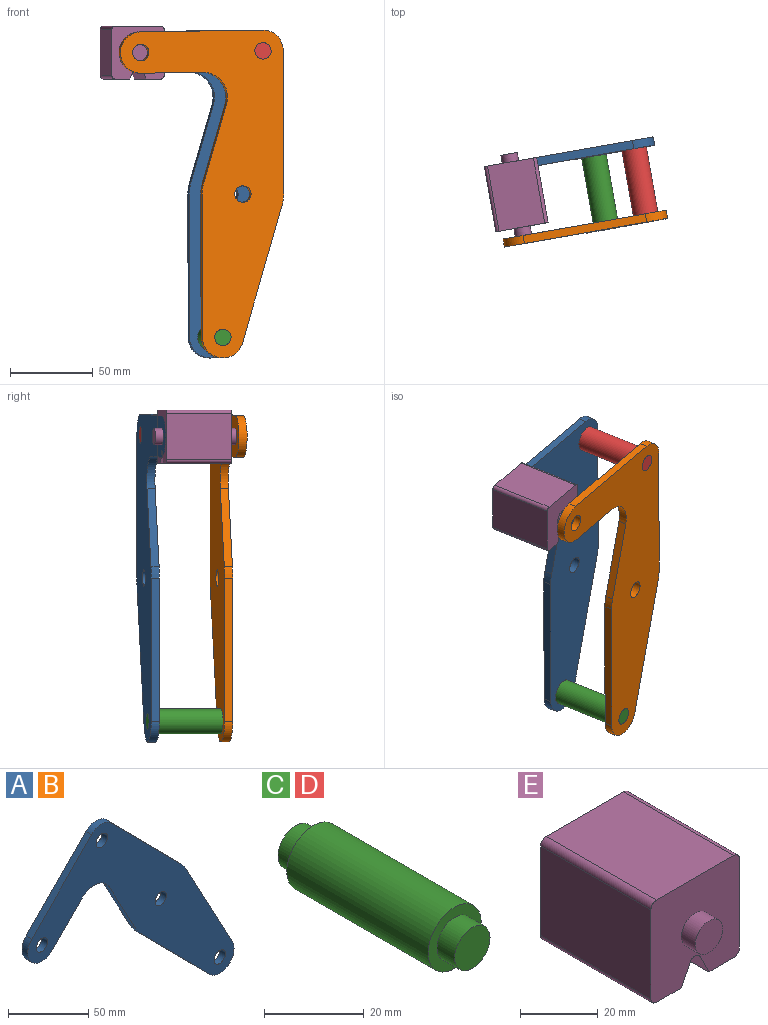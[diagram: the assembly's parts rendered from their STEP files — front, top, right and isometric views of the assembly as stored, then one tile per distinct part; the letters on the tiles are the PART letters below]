
ASSEMBLY  parts=5 mates=3
PART A: 18 faces, bbox 181.7x5x165.8 mm
  f0: plane 43.49x23.35mm, normal (-0.88,0,-0.47), area 246.8mm2, adj f1,f14,f16,f17
  f1: cylinder r=25mm len=5.75mm, axis (0,1,0), area 35.8mm2, adj f0,f2,f16,f17
  f2: plane 61.6x60.87mm, normal (-0.71,0,-0.7), area 433mm2, adj f1,f3,f16,f17
  f3: cylinder r=12.5mm len=21.39mm, axis (0,1,0), area 178.4mm2, adj f2,f4,f16,f17
  f4: plane 76.3x40.96mm, normal (0.88,0,0.47), area 433mm2, adj f3,f5,f16,f17
  f5: cylinder r=25mm len=5.75mm, axis (0,1,0), area 35.8mm2, adj f4,f6,f16,f17
  f6: plane 61.6x60.87mm, normal (0.71,0,0.7), area 433mm2, adj f5,f7,f16,f17
  f7: cylinder r=12.5mm len=17.78mm, axis (0,1,0), area 98.9mm2, adj f6,f8,f16,f17
  f8: plane 53.35x52.71mm, normal (-0.71,0,0.7), area 375mm2, adj f7,f9,f16,f17
  f9: cylinder r=12.5mm len=21.39mm, axis (0,1,0), area 196.3mm2, adj f8,f10,f16,f17
  f10: plane 26.86x26.54mm, normal (0.71,0,-0.7), area 188.8mm2, adj f9,f14,f16,f17
  f11: cylinder r=5mm len=10mm, axis (0,1,0), area 157.1mm2, adj f16,f17
  f12: cylinder r=5mm len=10mm, axis (0,1,0), area 157.1mm2, adj f16,f17
  f13: cylinder r=5mm len=10mm, axis (0,1,0), area 157.1mm2, adj f16,f17
  f14: cylinder r=15mm len=23.89mm, axis (0,1,0), area 140.2mm2, adj f0,f10,f16,f17
  f15: cylinder r=5mm len=10mm, axis (0,1,0), area 157.1mm2, adj f16,f17
  f16: plane 181.66x165.78mm, normal (0,-1,0), area 8710.1mm2, adj f0,f1,f2,f3,f4,f5,f6,f7
  f17: plane 181.66x165.78mm, normal (0,1,0), area 8710.1mm2, adj f0,f1,f2,f3,f4,f5,f6,f7
PART B: same geometry as A
PART C: 7 faces, bbox 15x50x15 mm
  f0: cylinder r=7.5mm len=40mm, axis (0,-1,0), area 1885mm2, adj f2,f5
  f1: cylinder r=5mm len=10mm, axis (0,1,0), area 157.1mm2, adj f2,f3
  f2: plane 15x15mm, normal (0,-1,0), area 98.2mm2, adj f0,f1
  f3: plane 10x10mm, normal (0,-1,0), area 78.5mm2, adj f1
  f4: cylinder r=5mm len=10mm, axis (0,-1,0), area 157.1mm2, adj f5,f6
  f5: plane 15x15mm, normal (0,1,0), area 98.2mm2, adj f0,f4
  f6: plane 10x10mm, normal (0,1,0), area 78.5mm2, adj f4
PART D: same geometry as C
PART E: 18 faces, bbox 32.1x50x32.1 mm
  f0: plane 40x28.08mm, normal (1,0,0), area 1123.1mm2, adj f4,f10,f13,f14
  f1: plane 40x9.04mm, normal (0,0,-1), area 361.6mm2, adj f2,f4,f10,f14
  f2: plane 40x6.42mm, normal (-0.89,0,-0.45), area 287.2mm2, adj f1,f4,f10,f15
  f3: plane 40x6.42mm, normal (0.89,0,-0.45), area 287.2mm2, adj f4,f5,f10,f15
  f4: plane 32.08x32.08mm, normal (0,-1,0), area 900.6mm2, adj f0,f1,f2,f3,f5,f6,f7,f9
  f5: plane 40x9.04mm, normal (0,0,-1), area 361.6mm2, adj f3,f4,f10,f16
  f6: plane 40x28.08mm, normal (0,0,1), area 1123.1mm2, adj f4,f10,f13,f17
  f7: plane 40x28.08mm, normal (-1,0,0), area 1123.1mm2, adj f4,f10,f16,f17
  f8: plane 10x10mm, normal (0,-1,0), area 78.5mm2, adj f9
  f9: cylinder r=5mm len=10mm, axis (0,1,0), area 157.1mm2, adj f4,f8
  f10: plane 32.08x32.08mm, normal (0,1,0), area 900.6mm2, adj f0,f1,f2,f3,f5,f6,f7,f12
  f11: plane 10x10mm, normal (0,1,0), area 78.5mm2, adj f12
  f12: cylinder r=5mm len=10mm, axis (0,-1,0), area 157.1mm2, adj f10,f11
  f13: cylinder r=2mm len=40mm, axis (0,1,0), area 125.7mm2, adj f0,f4,f6,f10
  f14: cylinder r=2mm len=40mm, axis (0,-1,0), area 125.7mm2, adj f0,f1,f4,f10
  f15: cylinder r=2mm len=40mm, axis (0,1,0), area 177.1mm2, adj f2,f3,f4,f10
  f16: cylinder r=2mm len=40mm, axis (0,1,0), area 125.7mm2, adj f4,f5,f7,f10
  f17: cylinder r=2mm len=40mm, axis (0,-1,0), area 125.7mm2, adj f4,f6,f7,f10
PLACE A rot(axis=(-0.09,0.97,0.21),45.6deg) t=(-53.46,15.83,-65.29)mm
PLACE B rot(axis=(-0.09,0.97,0.21),45.6deg) t=(-45.64,-28.48,-65.29)mm fixed
PLACE C rot(axis=(-0.09,0.97,0.21),45.6deg) t=(-69.89,-32.76,-238.55)mm
PLACE D rot(axis=(-0.09,0.97,0.21),45.6deg) t=(-45.64,-28.48,-65.29)mm
PLACE E rot(axis=(0,0,1),10deg) t=(-5.14,-16.27,3.23)mm
MATE revolute A.f3 <-> C.f0  axis (0.17,-0.98,0) through (-64.71,8.77,-151.92)mm
MATE revolute A.f7 <-> D.f0  axis (-0.17,0.98,0) through (-41.33,17.97,21.34)mm
MATE revolute B.f9 <-> E.f9  axis (-0.17,0.98,0) through (-107.37,-39.37,20.27)mm
